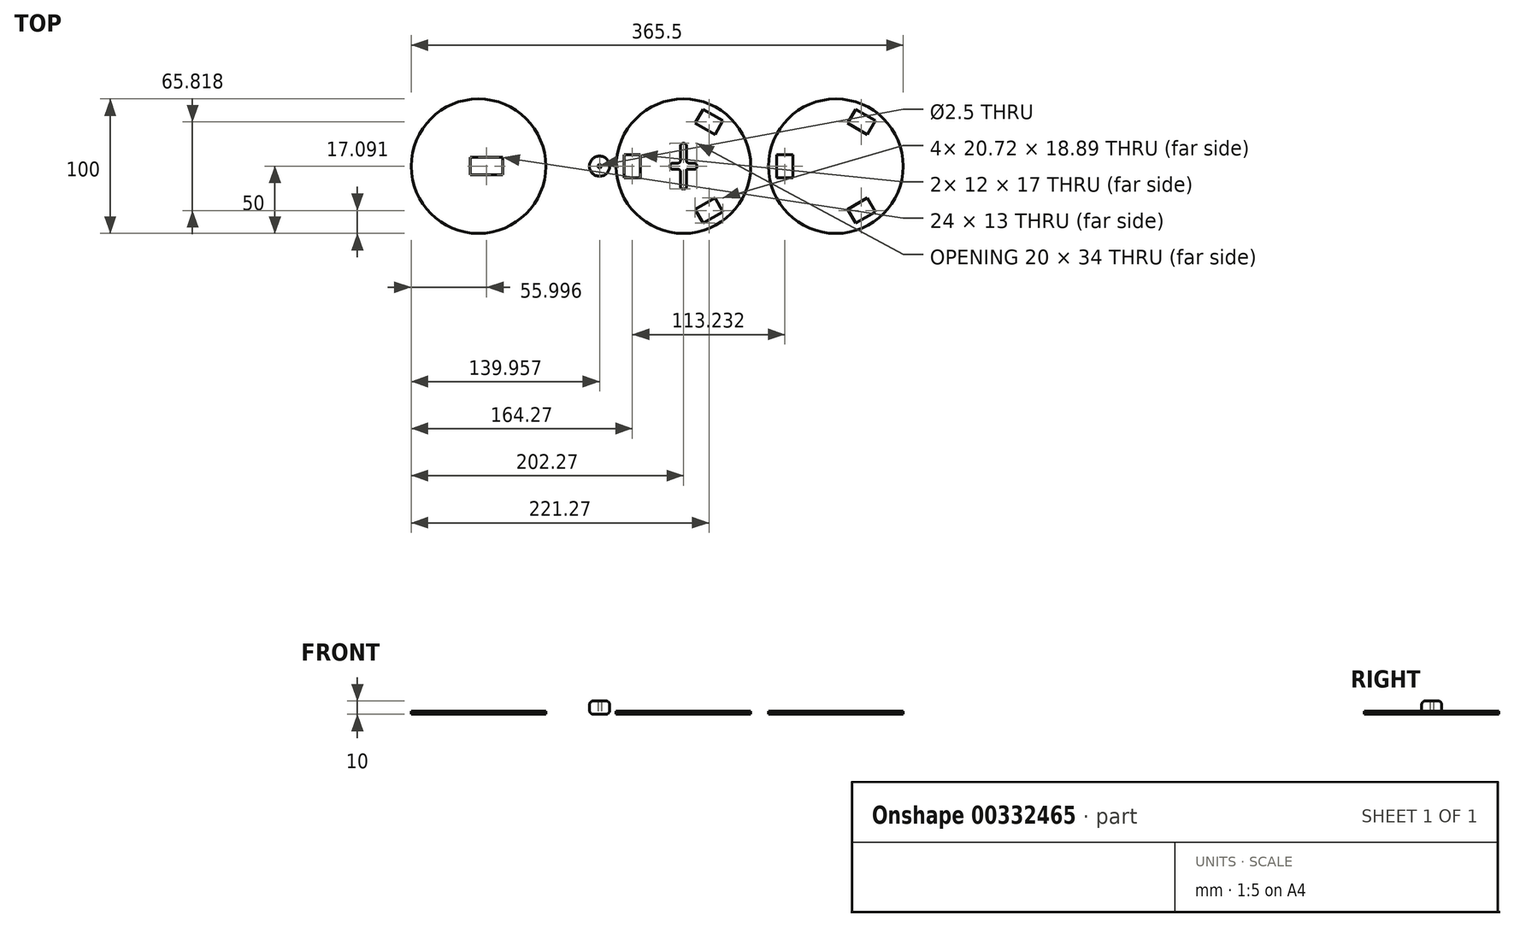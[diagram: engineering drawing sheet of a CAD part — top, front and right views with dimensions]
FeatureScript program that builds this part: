
annotation { "Feature Type Name" : "Feature", "Feature Type Description" : "" }
export const myFeature = defineFeature(function(context is Context, id is Id, definition is map)
    precondition{}
    {
        {
            var Q0;
            Q0=qCreatedBy(makeId("Top.planeOp"),FACE);
            var sketch = newSketch(context, id + "F0", { "sketchPlane" : qUnion([Q0])});
            skCircle(sketch, "E0", {"center": v(0, 0) * mm, "radius": 50 * mm});
            skLineSegment(sketch, "E1.bottom", {"start": v(-32, 8.5) * mm, "end": v(-44, 8.5) * mm});
            skLineSegment(sketch, "E1.top", {"start": v(-32, -8.5) * mm, "end": v(-44, -8.5) * mm});
            skLineSegment(sketch, "E1.left", {"start": v(-32, 8.5) * mm, "end": v(-32, -8.5) * mm});
            skLineSegment(sketch, "E1.right", {"start": v(-44, 8.5) * mm, "end": v(-44, -8.5) * mm});
            skLineSegment(sketch, "E2.bottom", {"start": v(-2.25, -17) * mm, "end": v(2.25, -17) * mm});
            skLineSegment(sketch, "E2.top", {"start": v(-2.25, 17) * mm, "end": v(2.25, 17) * mm});
            skLineSegment(sketch, "E2.left", {"start": v(-2.25, -17) * mm, "end": v(-2.25, -2.25) * mm});
            skLineSegment(sketch, "E2.right", {"start": v(2.25, -17) * mm, "end": v(2.25, -2.25) * mm});
            skLineSegment(sketch, "E3.top", {"start": v(-10, -2.25) * mm, "end": v(-2.25, -2.25) * mm});
            skLineSegment(sketch, "E3.left", {"start": v(-10, 2.25) * mm, "end": v(-10, -2.25) * mm});
            skLineSegment(sketch, "E3.right", {"start": v(10, 2.25) * mm, "end": v(10, -2.25) * mm});
            skLineSegment(sketch, "E4", {"start": v(-10, 2.25) * mm, "end": v(-2.25, 2.25) * mm});
            skLineSegment(sketch, "E5", {"start": v(-2.25, 2.25) * mm, "end": v(-2.25, 17) * mm});
            skLineSegment(sketch, "E6", {"start": v(2.25, 17) * mm, "end": v(2.25, 2.25) * mm});
            skLineSegment(sketch, "E7", {"start": v(2.25, 2.25) * mm, "end": v(10, 2.25) * mm});
            skLineSegment(sketch, "E8", {"start": v(10, -2.25) * mm, "end": v(2.25, -2.25) * mm});
            skLineSegment(sketch, "E9", {"start": v(2.25, -2.25) * mm, "end": v(2.25, -17) * mm});
            skLineSegment(sketch, "E10", {"start": v(-2.25, -2.25) * mm, "end": v(-10, -2.25) * mm});
            skLineSegment(sketch, "E11.trimOffspring", {"start": v(2.25, 2.25) * mm, "end": v(2.25, 17) * mm});
            skLineSegment(sketch, "E12.trimOffspring", {"start": v(2.25, -2.25) * mm, "end": v(10, -2.25) * mm});
            skCircle(sketch, "E13", {"center": v(-152.27, 0) * mm, "radius": 50 * mm});
            skLineSegment(sketch, "E14", {"start": v(-152.27, 0) * mm, "end": v(-146.27, 0) * mm});
            skLineSegment(sketch, "E15.bottom", {"start": v(-158.27, 6.5) * mm, "end": v(-134.27, 6.5) * mm});
            skLineSegment(sketch, "E15.top", {"start": v(-158.27, -6.5) * mm, "end": v(-134.27, -6.5) * mm});
            skLineSegment(sketch, "E15.left", {"start": v(-158.27, 6.5) * mm, "end": v(-158.27, -6.5) * mm});
            skLineSegment(sketch, "E15.right", {"start": v(-134.27, 6.5) * mm, "end": v(-134.27, -6.5) * mm});
            skPoint(sketch, "E15.middle", {"position": v(-146.27, 0) * mm});
            skCircle(sketch, "E16", {"center": v(-62.31, 0) * mm, "radius": 1.25 * mm});
            skCircle(sketch, "E17", {"center": v(-62.31, 0) * mm, "radius": 7.5 * mm});
            skLineSegment(sketch, "E18", {"start": v(-44, 7.5) * mm, "end": v(-32, 7.5) * mm});
            skPoint(sketch, "E19", {"position": v(-44, 0) * mm});
            skLineSegment(sketch, "E20.1.0", {"start": v(8.64, -31.96) * mm, "end": v(23.36, -23.46) * mm});
            skLineSegment(sketch, "E20.1.1", {"start": v(14.64, -42.36) * mm, "end": v(29.36, -33.86) * mm});
            skPoint(sketch, "E20.1.2", {"position": v(22, -38.1) * mm});
            skLineSegment(sketch, "E20.1.3", {"start": v(8.64, -31.96) * mm, "end": v(14.64, -42.36) * mm});
            skLineSegment(sketch, "E20.1.4", {"start": v(23.36, -23.46) * mm, "end": v(29.36, -33.86) * mm});
            skLineSegment(sketch, "E20.2.0", {"start": v(23.36, 23.46) * mm, "end": v(8.64, 31.96) * mm});
            skLineSegment(sketch, "E20.2.1", {"start": v(29.36, 33.86) * mm, "end": v(14.64, 42.36) * mm});
            skPoint(sketch, "E20.2.2", {"position": v(22, 38.1) * mm});
            skLineSegment(sketch, "E20.2.3", {"start": v(23.36, 23.46) * mm, "end": v(29.36, 33.86) * mm});
            skLineSegment(sketch, "E20.2.4", {"start": v(8.64, 31.96) * mm, "end": v(14.64, 42.36) * mm});
            skLineSegment(sketch, "E21.1.0.0", {"start": v(121.87, 31.96) * mm, "end": v(127.87, 42.36) * mm});
            skLineSegment(sketch, "E21.1.0.1", {"start": v(69.23, 7.5) * mm, "end": v(81.23, 7.5) * mm});
            skLineSegment(sketch, "E21.1.0.2", {"start": v(121.87, -31.96) * mm, "end": v(136.6, -23.46) * mm});
            skLineSegment(sketch, "E21.1.0.3", {"start": v(142.6, 33.86) * mm, "end": v(127.87, 42.36) * mm});
            skPoint(sketch, "E21.1.0.4", {"position": v(135.23, -38.1) * mm});
            skLineSegment(sketch, "E21.1.0.5", {"start": v(127.87, -42.36) * mm, "end": v(142.6, -33.86) * mm});
            skLineSegment(sketch, "E21.1.0.6", {"start": v(81.23, 8.5) * mm, "end": v(69.23, 8.5) * mm});
            skLineSegment(sketch, "E21.1.0.7", {"start": v(81.23, -8.5) * mm, "end": v(69.23, -8.5) * mm});
            skCircle(sketch, "E21.1.0.8", {"center": v(113.23, 0) * mm, "radius": 50 * mm});
            skLineSegment(sketch, "E21.1.0.10", {"start": v(136.6, 23.46) * mm, "end": v(142.6, 33.86) * mm});
            skLineSegment(sketch, "E21.1.0.11", {"start": v(136.6, 23.46) * mm, "end": v(121.87, 31.96) * mm});
            skLineSegment(sketch, "E21.1.0.12", {"start": v(121.87, -31.96) * mm, "end": v(127.87, -42.36) * mm});
            skLineSegment(sketch, "E21.1.0.13", {"start": v(136.6, -23.46) * mm, "end": v(142.6, -33.86) * mm});
            skLineSegment(sketch, "E21.1.0.14", {"start": v(81.23, 8.5) * mm, "end": v(81.23, -8.5) * mm});
            skLineSegment(sketch, "E21.1.0.15", {"start": v(69.23, 8.5) * mm, "end": v(69.23, -8.5) * mm});
            skPoint(sketch, "E21.1.0.16", {"position": v(135.23, 38.1) * mm});
            skPoint(sketch, "E21.1.0.18", {"position": v(69.23, 0) * mm});
            skLineSegment(sketch, "E21.direction1", {"start": v(-44, -8.5) * mm, "end": v(69.23, -8.5) * mm, "construction": true});
            skSolve(sketch);
        }
        {
            var Q0;
            Q0=makeQuery(id+"F0.imprint","IMPRINT",FACE,{"disambiguationData":[TD([[makeQuery(id+"F0.imprint","IMPRINT",EDGE,{"derivedFrom":sQuery(id+"F0.wireOp",EDGE,"E13")}),1.0]])]});
            var Q1;
            Q1=makeQuery(id+"F0.imprint","IMPRINT",FACE,{"disambiguationData":[TD([[makeQuery(id+"F0.imprint","IMPRINT",EDGE,{"derivedFrom":sQuery(id+"F0.wireOp",EDGE,"E0")}),1.0]])]});
            var Q2;
            Q2=makeQuery(id+"F0.imprint","IMPRINT",FACE,{"disambiguationData":[TD([[makeQuery(id+"F0.imprint","IMPRINT",EDGE,{"derivedFrom":sQuery(id+"F0.wireOp",EDGE,"E21.1.0.0")}),1.0]])]});
            extrude(context, id + "F1", {"entities" : qUnion([Q0, Q1, Q2]), "depth" : 2.24 * mm});
        }
        {
            var Q0;
            Q0=makeQuery(id+"F1.opExtrude","SWEPT_EDGE",EDGE,{"disambiguationData":[OSD([sQuery(id+"F0.wireOp",EDGE,"E2.top"),sQuery(id+"F0.wireOp",EDGE,"E11.trimOffspring")])]});
            var Q1;
            Q1=makeQuery(id+"F1.opExtrude","SWEPT_EDGE",EDGE,{"disambiguationData":[OSD([sQuery(id+"F0.wireOp",EDGE,"E3.right"),sQuery(id+"F0.wireOp",EDGE,"E7")])]});
            var Q2;
            Q2=makeQuery(id+"F1.opExtrude","SWEPT_EDGE",EDGE,{"disambiguationData":[OSD([sQuery(id+"F0.wireOp",EDGE,"E7"),sQuery(id+"F0.wireOp",EDGE,"E11.trimOffspring")])]});
            var Q3;
            Q3=makeQuery(id+"F1.opExtrude","SWEPT_EDGE",EDGE,{"disambiguationData":[OSD([sQuery(id+"F0.wireOp",EDGE,"E9"),sQuery(id+"F0.wireOp",EDGE,"E12.trimOffspring")])]});
            var Q4;
            Q4=makeQuery(id+"F1.opExtrude","SWEPT_EDGE",EDGE,{"disambiguationData":[OSD([sQuery(id+"F0.wireOp",EDGE,"E2.bottom"),sQuery(id+"F0.wireOp",EDGE,"E9")])]});
            var Q5;
            Q5=makeQuery(id+"F1.opExtrude","SWEPT_EDGE",EDGE,{"disambiguationData":[OSD([sQuery(id+"F0.wireOp",EDGE,"E2.top"),sQuery(id+"F0.wireOp",EDGE,"E5")])]});
            var Q6;
            Q6=makeQuery(id+"F1.opExtrude","SWEPT_EDGE",EDGE,{"disambiguationData":[OSD([sQuery(id+"F0.wireOp",EDGE,"E4"),sQuery(id+"F0.wireOp",EDGE,"E5")])]});
            var Q7;
            Q7=makeQuery(id+"F1.opExtrude","SWEPT_EDGE",EDGE,{"disambiguationData":[OSD([sQuery(id+"F0.wireOp",EDGE,"E3.left"),sQuery(id+"F0.wireOp",EDGE,"E4")])]});
            var Q8;
            Q8=makeQuery(id+"F1.opExtrude","SWEPT_EDGE",EDGE,{"disambiguationData":[OSD([sQuery(id+"F0.wireOp",EDGE,"E2.left"),sQuery(id+"F0.wireOp",EDGE,"E10")])]});
            var Q9;
            Q9=makeQuery(id+"F1.opExtrude","SWEPT_EDGE",EDGE,{"disambiguationData":[OSD([sQuery(id+"F0.wireOp",EDGE,"E3.left"),sQuery(id+"F0.wireOp",EDGE,"E10")])]});
            var Q10;
            Q10=makeQuery(id+"F1.opExtrude","SWEPT_EDGE",EDGE,{"disambiguationData":[OSD([sQuery(id+"F0.wireOp",EDGE,"E2.bottom"),sQuery(id+"F0.wireOp",EDGE,"E2.left")])]});
            var Q11;
            Q11=makeQuery(id+"F1.opExtrude","SWEPT_EDGE",EDGE,{"disambiguationData":[OSD([sQuery(id+"F0.wireOp",EDGE,"E3.right"),sQuery(id+"F0.wireOp",EDGE,"E12.trimOffspring")])]});
            fillet(context, id + "F2", {"entities" : qUnion([Q0, Q1, Q2, Q3, Q4, Q5, Q6, Q7, Q8, Q9, Q10, Q11]), "radius" : 2 * mm, "tangentPropagation" : true, "allowEdgeOverflow" : false});
        }
        {
            var Q0;
            Q0=makeQuery(id+"F0.imprint","IMPRINT",FACE,{"disambiguationData":[TD([[makeQuery(id+"F0.imprint","IMPRINT",EDGE,{"derivedFrom":sQuery(id+"F0.wireOp",EDGE,"E16")}),-1.0]])]});
            extrude(context, id + "F3", {"entities" : qUnion([Q0]), "depth" : 10 * mm});
        }
        {
            var Q0;
            Q0=makeQuery(id+"F3.opExtrude","CAP_EDGE",EDGE,{"disambiguationData":[OSD([sQuery(id+"F0.wireOp",EDGE,"E17")])],"isStart":false});
            var Q1;
            Q1=makeQuery(id+"F3.opExtrude","CAP_EDGE",EDGE,{"disambiguationData":[OSD([sQuery(id+"F0.wireOp",EDGE,"E17")])],"isStart":true});
            fillet(context, id + "F4", {"entities" : qUnion([Q0, Q1]), "radius" : 3 * mm, "tangentPropagation" : true, "allowEdgeOverflow" : false});
        }
    });
